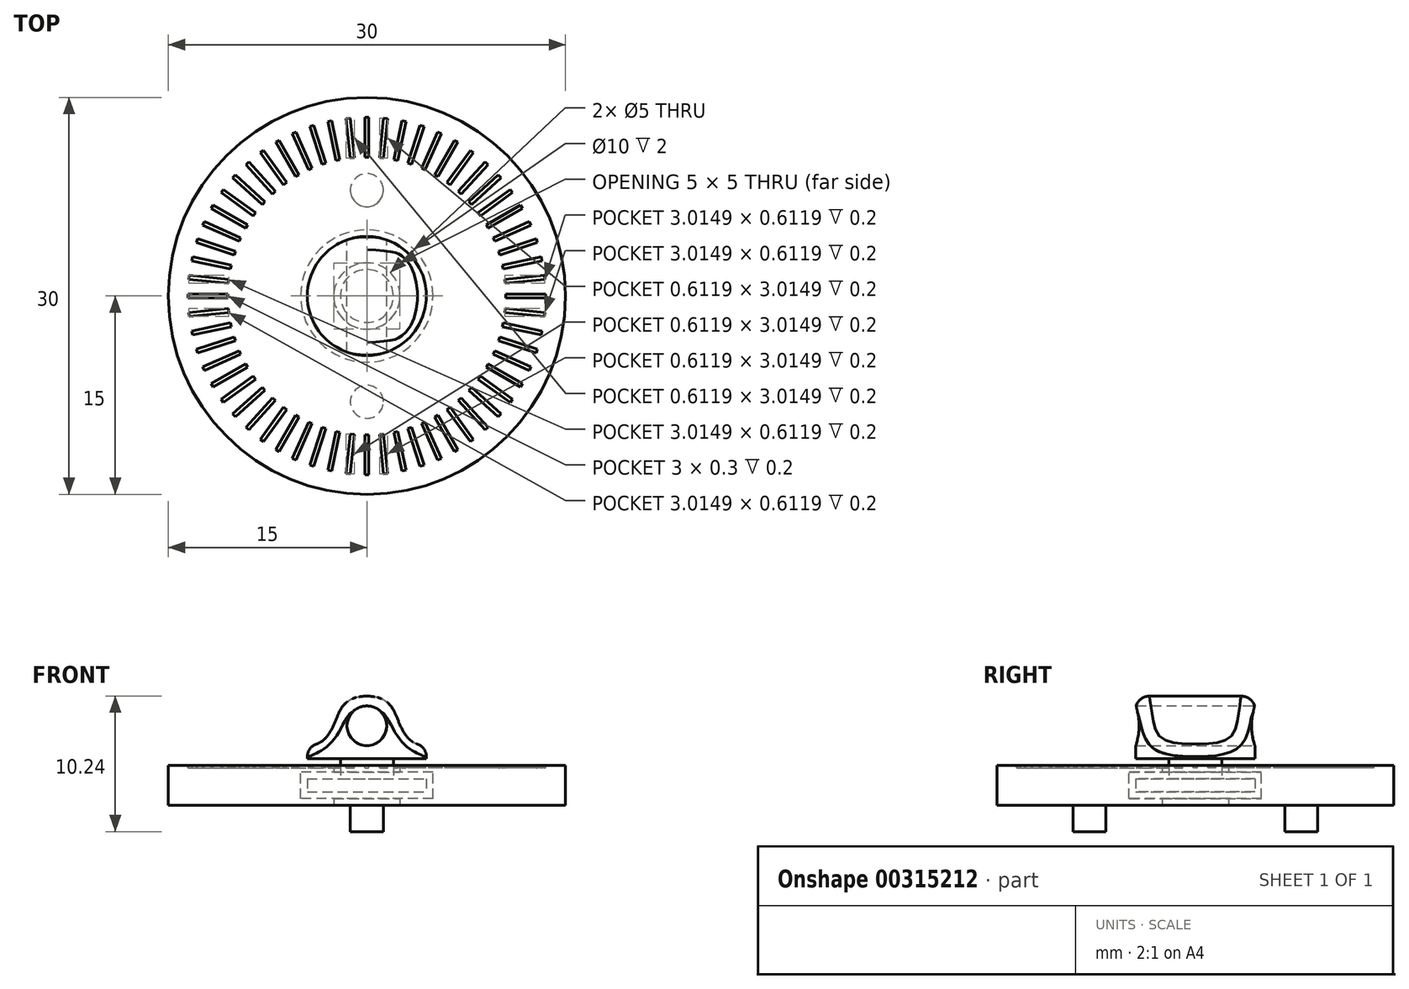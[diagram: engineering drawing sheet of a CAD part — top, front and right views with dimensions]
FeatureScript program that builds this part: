
annotation { "Feature Type Name" : "Feature", "Feature Type Description" : "" }
export const myFeature = defineFeature(function(context is Context, id is Id, definition is map)
    precondition{}
    {
        {
            var Q0;
            Q0=qCreatedBy(makeId("Top.planeOp"),FACE);
            var sketch = newSketch(context, id + "F0", { "sketchPlane" : qUnion([Q0])});
            skCircle(sketch, "E0", {"center": v(0, 0) * mm, "radius": 15 * mm});
            skCircle(sketch, "E1", {"center": v(0, 0) * mm, "radius": 2.5 * mm});
            skSolve(sketch);
        }
        {
            var Q0;
            Q0=makeQuery(id+"F0.imprint","IMPRINT",FACE,{"disambiguationData":[TD([[makeQuery(id+"F0.imprint","IMPRINT",EDGE,{"derivedFrom":sQuery(id+"F0.wireOp",EDGE,"E0")}),1.0]])]});
            extrude(context, id + "F1", {"entities" : qUnion([Q0]), "depth" : 3 * mm, "offsetDistance" : 25 * mm});
        }
        {
            var Q0;
            Q0=qCreatedBy(makeId("Front.planeOp"),FACE);
            var sketch = newSketch(context, id + "F2", { "sketchPlane" : qUnion([Q0])});
            skLineSegment(sketch, "E2.0", {"start": v(-2.5, 3) * mm, "end": v(2.5, 3) * mm, "construction": true});
            skLineSegment(sketch, "E3.0", {"start": v(-2.5, 0) * mm, "end": v(2.5, 0) * mm, "construction": true});
            skLineSegment(sketch, "E4", {"start": v(0, 0) * mm, "end": v(0, 16.06) * mm, "construction": true});
            skLineSegment(sketch, "E5", {"start": v(-2, 2) * mm, "end": v(-4.5, 2) * mm});
            skLineSegment(sketch, "E6", {"start": v(-4.5, 2) * mm, "end": v(-4.5, 1) * mm});
            skLineSegment(sketch, "E7", {"start": v(-4.5, 1) * mm, "end": v(0, 1) * mm});
            skLineSegment(sketch, "E8", {"start": v(-2, 2) * mm, "end": v(-2, 3.5) * mm});
            skLineSegment(sketch, "E9", {"start": v(0, 1) * mm, "end": v(0, 0) * mm, "construction": true});
            skLineSegment(sketch, "E10", {"start": v(-2, 3.5) * mm, "end": v(-4.5, 3.5) * mm});
            skLineSegment(sketch, "E11", {"start": v(-4.5, 3.5) * mm, "end": v(-4.5, 4.5) * mm});
            skLineSegment(sketch, "E12", {"start": v(-4.5, 4.5) * mm, "end": v(0, 4.5) * mm});
            skLineSegment(sketch, "E13", {"start": v(0, 4.5) * mm, "end": v(0, 1) * mm});
            skLineSegment(sketch, "E14", {"start": v(-4.5, 3.5) * mm, "end": v(-4.5, 3) * mm, "construction": true});
            skSolve(sketch);
        }
        {
            var Q0;
            Q0=qCreatedBy(makeId("Front.planeOp"),FACE);
            var sketch = newSketch(context, id + "F3", { "sketchPlane" : qUnion([Q0])});
            skLineSegment(sketch, "E15.0", {"start": v(-2, 2) * mm, "end": v(-2, 3.5) * mm, "construction": true});
            skLineSegment(sketch, "E16", {"start": v(-2, 2.5) * mm, "end": v(-5, 2.5) * mm});
            skLineSegment(sketch, "E17", {"start": v(-5, 2.5) * mm, "end": v(-5, 0.5) * mm});
            skLineSegment(sketch, "E18", {"start": v(-5, 0.5) * mm, "end": v(0, 0.5) * mm});
            skLineSegment(sketch, "E19", {"start": v(-2, 2.5) * mm, "end": v(-2, 2) * mm});
            skLineSegment(sketch, "E20.0", {"start": v(0, 0) * mm, "end": v(0, 16.06) * mm, "construction": true});
            skLineSegment(sketch, "E21", {"start": v(-2, 2.5) * mm, "end": v(0, 2.5) * mm});
            skLineSegment(sketch, "E22", {"start": v(0, 2.5) * mm, "end": v(0, 0.5) * mm});
            skSolve(sketch);
        }
        {
            var Q0;
            Q0=makeQuery(id+"F3.imprint","IMPRINT",FACE,{"disambiguationData":[TD([[makeQuery(id+"F3.imprint","IMPRINT",EDGE,{"derivedFrom":sQuery(id+"F3.wireOp",EDGE,"E16")}),1.0]])]});
            var Q1;
            Q1=sQuery(id+"F2.wireOp",EDGE,"E4");
            revolve(context, id + "F4", {"operationType" : NewBodyOperationType.REMOVE, "surfaceOperationType" : NewSurfaceOperationType.NEW, "entities" : qUnion([Q0]), "axis" : qUnion([Q1]), "revolveType" : RevolveType.FULL, "oppositeDirection" : true});
        }
        {
            var Q0;
            Q0=makeQuery(id+"F2.imprint","IMPRINT",FACE,{"disambiguationData":[TD([[makeQuery(id+"F2.imprint","IMPRINT",EDGE,{"derivedFrom":sQuery(id+"F2.wireOp",EDGE,"E5")}),1.0]])]});
            var Q1;
            Q1=sQuery(id+"F2.wireOp",EDGE,"E4");
            revolve(context, id + "F5", {"surfaceOperationType" : NewSurfaceOperationType.NEW, "entities" : qUnion([Q0]), "axis" : qUnion([Q1]), "revolveType" : RevolveType.FULL});
        }
        {
            var Q0;
            Q0=qCreatedBy(makeId("Front.planeOp"),FACE);
            var sketch = newSketch(context, id + "F6", { "sketchPlane" : qUnion([Q0])});
            skLineSegment(sketch, "E23.0", {"start": v(4.5, 4.5) * mm, "end": v(-4.5, 4.5) * mm});
            skCircle(sketch, "E24", {"center": v(0, 6) * mm, "radius": 1.5 * mm});
            skLineSegment(sketch, "E25.0", {"start": v(0, 0) * mm, "end": v(0, 16.06) * mm, "construction": true});
            skFitSpline(sketch, "E26", {"points": [v(0, 8.24) * mm, v(-2.5, 6.08) * mm, v(-4.5, 4.5) * mm], "startDerivative": vector(-10.34, 0) * mm, "endDerivative": vector(-7.09, 0) * mm});
            skLineSegment(sketch, "E27", {"start": v(0, 8.24) * mm, "end": v(-1.84, 8.24) * mm, "construction": true});
            skFitSpline(sketch, "E28.MirrorCS", {"points": [v(0, 8.24) * mm, v(2.5, 6.08) * mm, v(4.5, 4.5) * mm], "startDerivative": vector(10.34, 0) * mm, "endDerivative": vector(7.09, 0) * mm});
            skLineSegment(sketch, "E29.bottom", {"start": v(-1.1, 4.5) * mm, "end": v(1.14, 4.5) * mm});
            skLineSegment(sketch, "E29.top", {"start": v(-1.1, 3.86) * mm, "end": v(1.14, 3.86) * mm});
            skLineSegment(sketch, "E29.left", {"start": v(-1.1, 4.5) * mm, "end": v(-1.1, 3.86) * mm});
            skLineSegment(sketch, "E29.right", {"start": v(1.14, 4.5) * mm, "end": v(1.14, 3.86) * mm});
            skSolve(sketch);
        }
        {
            var Q0;
            {var subQ1=sQuery(id+"F6.wireOp",EDGE,"E24");Q0=makeQuery(id+"F6.imprint","IMPRINT",FACE,{"disambiguationData":[TD([[makeQuery(id+"F6.imprint","IMPRINT",EDGE,{"derivedFrom":subQ1}),-1.0]])]});}
            var Q1;
            Q1=makeQuery(id+"F6.imprint","IMPRINT",FACE,{"disambiguationData":[TD([[makeQuery(id+"F6.imprint","IMPRINT",EDGE,{"derivedFrom":sQuery(id+"F6.wireOp",EDGE,"E29.top")}),1.0]])]});
            var Q2;
            Q2=makeQuery(id+"F5.opRevolve","SWEPT_FACE",FACE,{"disambiguationData":[OSD([sQuery(id+"F2.wireOp",EDGE,"E11")])]});
            var Q3;
            Q3=makeQuery(id+"F5.opRevolve","SWEPT_FACE",FACE,{"disambiguationData":[OSD([sQuery(id+"F2.wireOp",EDGE,"E11")])]});
            extrude(context, id + "F7", {"entities" : qUnion([Q0, Q1]), "operationType" : NewBodyOperationType.ADD, "endBound" : BoundingType.UP_TO_SURFACE, "depth" : 25 * mm, "endBoundEntityFace" : qUnion([Q2]), "offsetDistance" : 25 * mm, "hasSecondDirection" : true, "secondDirectionBound" : BoundingType.UP_TO_SURFACE, "secondDirectionOppositeDirection" : true, "secondDirectionDepth" : 25 * mm, "secondDirectionBoundEntityFace" : qUnion([Q3])});
        }
        {
            var Q0;
            Q0=makeQuery(id+"F1.opExtrude","CAP_FACE",FACE,{"disambiguationData":[OSD([sQuery(id+"F0.wireOp",EDGE,"E0"),sQuery(id+"F0.wireOp",EDGE,"E1")])],"isStart":false});
            var sketch = newSketch(context, id + "F8", { "sketchPlane" : qUnion([Q0])});
            skLineSegment(sketch, "E30.bottom", {"start": v(-0.15, 13.5) * mm, "end": v(0.15, 13.5) * mm});
            skLineSegment(sketch, "E30.top", {"start": v(-0.15, 10.5) * mm, "end": v(0.15, 10.5) * mm});
            skLineSegment(sketch, "E30.left", {"start": v(-0.15, 13.5) * mm, "end": v(-0.15, 10.5) * mm});
            skLineSegment(sketch, "E30.right", {"start": v(0.15, 13.5) * mm, "end": v(0.15, 10.5) * mm});
            skPoint(sketch, "E31", {"position": v(0, 13.5) * mm});
            skLineSegment(sketch, "E32.1.0", {"start": v(-1.56, 13.41) * mm, "end": v(-1.25, 10.43) * mm});
            skLineSegment(sketch, "E32.1.1", {"start": v(-1.26, 13.44) * mm, "end": v(-0.95, 10.46) * mm});
            skPoint(sketch, "E32.1.2", {"position": v(-1.41, 13.43) * mm});
            skLineSegment(sketch, "E32.1.3", {"start": v(-1.56, 13.41) * mm, "end": v(-1.26, 13.44) * mm});
            skLineSegment(sketch, "E32.1.4", {"start": v(-1.25, 10.43) * mm, "end": v(-0.95, 10.46) * mm});
            skLineSegment(sketch, "E32.2.0", {"start": v(-2.95, 13.17) * mm, "end": v(-2.33, 10.24) * mm});
            skLineSegment(sketch, "E32.2.1", {"start": v(-2.66, 13.24) * mm, "end": v(-2.04, 10.3) * mm});
            skPoint(sketch, "E32.2.2", {"position": v(-2.8, 13.2) * mm});
            skLineSegment(sketch, "E32.2.3", {"start": v(-2.95, 13.17) * mm, "end": v(-2.66, 13.24) * mm});
            skLineSegment(sketch, "E32.2.4", {"start": v(-2.33, 10.24) * mm, "end": v(-2.04, 10.3) * mm});
            skPoint(sketch, "E32.center", {"position": v(0, 0) * mm});
            skLineSegment(sketch, "E33.2.3.0", {"start": v(-4.31, 12.8) * mm, "end": v(-3.39, 9.94) * mm});
            skLineSegment(sketch, "E33.3.3.0", {"start": v(-4.03, 12.89) * mm, "end": v(-3.1, 10.03) * mm});
            skPoint(sketch, "E33.6.3.0", {"position": v(-4.17, 12.84) * mm});
            skLineSegment(sketch, "E33.7.3.0", {"start": v(-4.31, 12.8) * mm, "end": v(-4.03, 12.89) * mm});
            skLineSegment(sketch, "E33.10.3.0", {"start": v(-3.39, 9.94) * mm, "end": v(-3.1, 10.03) * mm});
            skLineSegment(sketch, "E33.2.4.0", {"start": v(-5.63, 12.27) * mm, "end": v(-4.4, 9.53) * mm});
            skLineSegment(sketch, "E33.3.4.0", {"start": v(-5.35, 12.4) * mm, "end": v(-4.13, 9.65) * mm});
            skPoint(sketch, "E33.6.4.0", {"position": v(-5.5, 12.33) * mm});
            skLineSegment(sketch, "E33.7.4.0", {"start": v(-5.63, 12.27) * mm, "end": v(-5.35, 12.4) * mm});
            skLineSegment(sketch, "E33.10.4.0", {"start": v(-4.4, 9.53) * mm, "end": v(-4.13, 9.65) * mm});
            skLineSegment(sketch, "E33.2.5.0", {"start": v(-6.88, 11.62) * mm, "end": v(-5.38, 9.02) * mm});
            skLineSegment(sketch, "E33.3.5.0", {"start": v(-6.62, 11.77) * mm, "end": v(-5.12, 9.17) * mm});
            skPoint(sketch, "E33.6.5.0", {"position": v(-6.75, 11.7) * mm});
            skLineSegment(sketch, "E33.7.5.0", {"start": v(-6.88, 11.62) * mm, "end": v(-6.62, 11.77) * mm});
            skLineSegment(sketch, "E33.10.5.0", {"start": v(-5.38, 9.02) * mm, "end": v(-5.12, 9.17) * mm});
            skLineSegment(sketch, "E33.2.6.0", {"start": v(-8.06, 10.83) * mm, "end": v(-6.3, 8.4) * mm});
            skLineSegment(sketch, "E33.3.6.0", {"start": v(-7.81, 11) * mm, "end": v(-6.05, 8.58) * mm});
            skPoint(sketch, "E33.6.6.0", {"position": v(-7.94, 10.92) * mm});
            skLineSegment(sketch, "E33.7.6.0", {"start": v(-8.06, 10.83) * mm, "end": v(-7.81, 11) * mm});
            skLineSegment(sketch, "E33.10.6.0", {"start": v(-6.3, 8.4) * mm, "end": v(-6.05, 8.58) * mm});
            skLineSegment(sketch, "E33.2.7.0", {"start": v(-9.14, 9.93) * mm, "end": v(-7.14, 7.7) * mm});
            skLineSegment(sketch, "E33.3.7.0", {"start": v(-8.92, 10.13) * mm, "end": v(-6.91, 7.9) * mm});
            skPoint(sketch, "E33.6.7.0", {"position": v(-9.03, 10.03) * mm});
            skLineSegment(sketch, "E33.7.7.0", {"start": v(-9.14, 9.93) * mm, "end": v(-8.92, 10.13) * mm});
            skLineSegment(sketch, "E33.10.7.0", {"start": v(-7.14, 7.7) * mm, "end": v(-6.91, 7.9) * mm});
            skLineSegment(sketch, "E33.2.8.0", {"start": v(-10.13, 8.92) * mm, "end": v(-7.9, 6.91) * mm});
            skLineSegment(sketch, "E33.3.8.0", {"start": v(-9.93, 9.14) * mm, "end": v(-7.7, 7.14) * mm});
            skPoint(sketch, "E33.6.8.0", {"position": v(-10.03, 9.03) * mm});
            skLineSegment(sketch, "E33.7.8.0", {"start": v(-10.13, 8.92) * mm, "end": v(-9.93, 9.14) * mm});
            skLineSegment(sketch, "E33.10.8.0", {"start": v(-7.9, 6.91) * mm, "end": v(-7.7, 7.14) * mm});
            skLineSegment(sketch, "E33.2.9.0", {"start": v(-11, 7.81) * mm, "end": v(-8.58, 6.05) * mm});
            skLineSegment(sketch, "E33.3.9.0", {"start": v(-10.83, 8.06) * mm, "end": v(-8.4, 6.3) * mm});
            skPoint(sketch, "E33.6.9.0", {"position": v(-10.92, 7.94) * mm});
            skLineSegment(sketch, "E33.7.9.0", {"start": v(-11, 7.81) * mm, "end": v(-10.83, 8.06) * mm});
            skLineSegment(sketch, "E33.10.9.0", {"start": v(-8.58, 6.05) * mm, "end": v(-8.4, 6.3) * mm});
            skLineSegment(sketch, "E34.2.10.0", {"start": v(-11.77, 6.62) * mm, "end": v(-9.17, 5.12) * mm});
            skLineSegment(sketch, "E34.3.10.0", {"start": v(-11.62, 6.88) * mm, "end": v(-9.02, 5.38) * mm});
            skPoint(sketch, "E34.6.10.0", {"position": v(-11.7, 6.75) * mm});
            skLineSegment(sketch, "E34.7.10.0", {"start": v(-11.77, 6.62) * mm, "end": v(-11.62, 6.88) * mm});
            skLineSegment(sketch, "E34.10.10.0", {"start": v(-9.17, 5.12) * mm, "end": v(-9.02, 5.38) * mm});
            skLineSegment(sketch, "E34.2.11.0", {"start": v(-12.4, 5.35) * mm, "end": v(-9.65, 4.13) * mm});
            skLineSegment(sketch, "E34.3.11.0", {"start": v(-12.27, 5.63) * mm, "end": v(-9.53, 4.4) * mm});
            skPoint(sketch, "E34.6.11.0", {"position": v(-12.33, 5.5) * mm});
            skLineSegment(sketch, "E34.7.11.0", {"start": v(-12.4, 5.35) * mm, "end": v(-12.27, 5.63) * mm});
            skLineSegment(sketch, "E34.10.11.0", {"start": v(-9.65, 4.13) * mm, "end": v(-9.53, 4.4) * mm});
            skLineSegment(sketch, "E34.2.12.0", {"start": v(-12.89, 4.03) * mm, "end": v(-10.03, 3.1) * mm});
            skLineSegment(sketch, "E34.3.12.0", {"start": v(-12.8, 4.31) * mm, "end": v(-9.94, 3.39) * mm});
            skPoint(sketch, "E34.6.12.0", {"position": v(-12.84, 4.17) * mm});
            skLineSegment(sketch, "E34.7.12.0", {"start": v(-12.89, 4.03) * mm, "end": v(-12.8, 4.31) * mm});
            skLineSegment(sketch, "E34.10.12.0", {"start": v(-10.03, 3.1) * mm, "end": v(-9.94, 3.39) * mm});
            skLineSegment(sketch, "E34.2.13.0", {"start": v(-13.24, 2.66) * mm, "end": v(-10.3, 2.04) * mm});
            skLineSegment(sketch, "E34.3.13.0", {"start": v(-13.17, 2.95) * mm, "end": v(-10.24, 2.33) * mm});
            skPoint(sketch, "E34.6.13.0", {"position": v(-13.2, 2.8) * mm});
            skLineSegment(sketch, "E34.7.13.0", {"start": v(-13.24, 2.66) * mm, "end": v(-13.17, 2.95) * mm});
            skLineSegment(sketch, "E34.10.13.0", {"start": v(-10.3, 2.04) * mm, "end": v(-10.24, 2.33) * mm});
            skLineSegment(sketch, "E34.2.14.0", {"start": v(-13.44, 1.26) * mm, "end": v(-10.46, 0.95) * mm});
            skLineSegment(sketch, "E34.3.14.0", {"start": v(-13.41, 1.56) * mm, "end": v(-10.43, 1.25) * mm});
            skPoint(sketch, "E34.6.14.0", {"position": v(-13.43, 1.41) * mm});
            skLineSegment(sketch, "E34.7.14.0", {"start": v(-13.44, 1.26) * mm, "end": v(-13.41, 1.56) * mm});
            skLineSegment(sketch, "E34.10.14.0", {"start": v(-10.46, 0.95) * mm, "end": v(-10.43, 1.25) * mm});
            skLineSegment(sketch, "E34.2.15.0", {"start": v(-13.5, -0.15) * mm, "end": v(-10.5, -0.15) * mm});
            skLineSegment(sketch, "E34.3.15.0", {"start": v(-13.5, 0.15) * mm, "end": v(-10.5, 0.15) * mm});
            skPoint(sketch, "E34.6.15.0", {"position": v(-13.5, 0) * mm});
            skLineSegment(sketch, "E34.7.15.0", {"start": v(-13.5, -0.15) * mm, "end": v(-13.5, 0.15) * mm});
            skLineSegment(sketch, "E34.10.15.0", {"start": v(-10.5, -0.15) * mm, "end": v(-10.5, 0.15) * mm});
            skLineSegment(sketch, "E34.2.16.0", {"start": v(-13.41, -1.56) * mm, "end": v(-10.43, -1.25) * mm});
            skLineSegment(sketch, "E34.3.16.0", {"start": v(-13.44, -1.26) * mm, "end": v(-10.46, -0.95) * mm});
            skPoint(sketch, "E34.6.16.0", {"position": v(-13.43, -1.41) * mm});
            skLineSegment(sketch, "E34.7.16.0", {"start": v(-13.41, -1.56) * mm, "end": v(-13.44, -1.26) * mm});
            skLineSegment(sketch, "E34.10.16.0", {"start": v(-10.43, -1.25) * mm, "end": v(-10.46, -0.95) * mm});
            skLineSegment(sketch, "E34.2.17.0", {"start": v(-13.17, -2.95) * mm, "end": v(-10.24, -2.33) * mm});
            skLineSegment(sketch, "E34.3.17.0", {"start": v(-13.24, -2.66) * mm, "end": v(-10.3, -2.04) * mm});
            skPoint(sketch, "E34.6.17.0", {"position": v(-13.2, -2.8) * mm});
            skLineSegment(sketch, "E34.7.17.0", {"start": v(-13.17, -2.95) * mm, "end": v(-13.24, -2.66) * mm});
            skLineSegment(sketch, "E34.10.17.0", {"start": v(-10.24, -2.33) * mm, "end": v(-10.3, -2.04) * mm});
            skLineSegment(sketch, "E34.2.18.0", {"start": v(-12.8, -4.31) * mm, "end": v(-9.94, -3.39) * mm});
            skLineSegment(sketch, "E34.3.18.0", {"start": v(-12.89, -4.03) * mm, "end": v(-10.03, -3.1) * mm});
            skPoint(sketch, "E34.6.18.0", {"position": v(-12.84, -4.17) * mm});
            skLineSegment(sketch, "E34.7.18.0", {"start": v(-12.8, -4.31) * mm, "end": v(-12.89, -4.03) * mm});
            skLineSegment(sketch, "E34.10.18.0", {"start": v(-9.94, -3.39) * mm, "end": v(-10.03, -3.1) * mm});
            skLineSegment(sketch, "E34.2.19.0", {"start": v(-12.27, -5.63) * mm, "end": v(-9.53, -4.4) * mm});
            skLineSegment(sketch, "E34.3.19.0", {"start": v(-12.4, -5.35) * mm, "end": v(-9.65, -4.13) * mm});
            skPoint(sketch, "E34.6.19.0", {"position": v(-12.33, -5.5) * mm});
            skLineSegment(sketch, "E34.7.19.0", {"start": v(-12.27, -5.63) * mm, "end": v(-12.4, -5.35) * mm});
            skLineSegment(sketch, "E34.10.19.0", {"start": v(-9.53, -4.4) * mm, "end": v(-9.65, -4.13) * mm});
            skLineSegment(sketch, "E35.2.20.0", {"start": v(-11.62, -6.88) * mm, "end": v(-9.02, -5.38) * mm});
            skLineSegment(sketch, "E35.3.20.0", {"start": v(-11.77, -6.62) * mm, "end": v(-9.17, -5.12) * mm});
            skPoint(sketch, "E35.6.20.0", {"position": v(-11.7, -6.75) * mm});
            skLineSegment(sketch, "E35.7.20.0", {"start": v(-11.62, -6.88) * mm, "end": v(-11.77, -6.62) * mm});
            skLineSegment(sketch, "E35.10.20.0", {"start": v(-9.02, -5.38) * mm, "end": v(-9.17, -5.12) * mm});
            skLineSegment(sketch, "E35.2.21.0", {"start": v(-10.83, -8.06) * mm, "end": v(-8.4, -6.3) * mm});
            skLineSegment(sketch, "E35.3.21.0", {"start": v(-11, -7.81) * mm, "end": v(-8.58, -6.05) * mm});
            skPoint(sketch, "E35.6.21.0", {"position": v(-10.92, -7.94) * mm});
            skLineSegment(sketch, "E35.7.21.0", {"start": v(-10.83, -8.06) * mm, "end": v(-11, -7.81) * mm});
            skLineSegment(sketch, "E35.10.21.0", {"start": v(-8.4, -6.3) * mm, "end": v(-8.58, -6.05) * mm});
            skLineSegment(sketch, "E35.2.22.0", {"start": v(-9.93, -9.14) * mm, "end": v(-7.7, -7.14) * mm});
            skLineSegment(sketch, "E35.3.22.0", {"start": v(-10.13, -8.92) * mm, "end": v(-7.9, -6.91) * mm});
            skPoint(sketch, "E35.6.22.0", {"position": v(-10.03, -9.03) * mm});
            skLineSegment(sketch, "E35.7.22.0", {"start": v(-9.93, -9.14) * mm, "end": v(-10.13, -8.92) * mm});
            skLineSegment(sketch, "E35.10.22.0", {"start": v(-7.7, -7.14) * mm, "end": v(-7.9, -6.91) * mm});
            skLineSegment(sketch, "E35.2.23.0", {"start": v(-8.92, -10.13) * mm, "end": v(-6.91, -7.9) * mm});
            skLineSegment(sketch, "E35.3.23.0", {"start": v(-9.14, -9.93) * mm, "end": v(-7.14, -7.7) * mm});
            skPoint(sketch, "E35.6.23.0", {"position": v(-9.03, -10.03) * mm});
            skLineSegment(sketch, "E35.7.23.0", {"start": v(-8.92, -10.13) * mm, "end": v(-9.14, -9.93) * mm});
            skLineSegment(sketch, "E35.10.23.0", {"start": v(-6.91, -7.9) * mm, "end": v(-7.14, -7.7) * mm});
            skLineSegment(sketch, "E35.2.24.0", {"start": v(-7.81, -11) * mm, "end": v(-6.05, -8.58) * mm});
            skLineSegment(sketch, "E35.3.24.0", {"start": v(-8.06, -10.83) * mm, "end": v(-6.3, -8.4) * mm});
            skPoint(sketch, "E35.6.24.0", {"position": v(-7.94, -10.92) * mm});
            skLineSegment(sketch, "E35.7.24.0", {"start": v(-7.81, -11) * mm, "end": v(-8.06, -10.83) * mm});
            skLineSegment(sketch, "E35.10.24.0", {"start": v(-6.05, -8.58) * mm, "end": v(-6.3, -8.4) * mm});
            skLineSegment(sketch, "E35.2.25.0", {"start": v(-6.62, -11.77) * mm, "end": v(-5.12, -9.17) * mm});
            skLineSegment(sketch, "E35.3.25.0", {"start": v(-6.88, -11.62) * mm, "end": v(-5.38, -9.02) * mm});
            skPoint(sketch, "E35.6.25.0", {"position": v(-6.75, -11.7) * mm});
            skLineSegment(sketch, "E35.7.25.0", {"start": v(-6.62, -11.77) * mm, "end": v(-6.88, -11.62) * mm});
            skLineSegment(sketch, "E35.10.25.0", {"start": v(-5.12, -9.17) * mm, "end": v(-5.38, -9.02) * mm});
            skLineSegment(sketch, "E35.2.26.0", {"start": v(-5.35, -12.4) * mm, "end": v(-4.13, -9.65) * mm});
            skLineSegment(sketch, "E35.3.26.0", {"start": v(-5.63, -12.27) * mm, "end": v(-4.4, -9.53) * mm});
            skPoint(sketch, "E35.6.26.0", {"position": v(-5.5, -12.33) * mm});
            skLineSegment(sketch, "E35.7.26.0", {"start": v(-5.35, -12.4) * mm, "end": v(-5.63, -12.27) * mm});
            skLineSegment(sketch, "E35.10.26.0", {"start": v(-4.13, -9.65) * mm, "end": v(-4.4, -9.53) * mm});
            skLineSegment(sketch, "E35.2.27.0", {"start": v(-4.03, -12.89) * mm, "end": v(-3.1, -10.03) * mm});
            skLineSegment(sketch, "E35.3.27.0", {"start": v(-4.31, -12.8) * mm, "end": v(-3.39, -9.94) * mm});
            skPoint(sketch, "E35.6.27.0", {"position": v(-4.17, -12.84) * mm});
            skLineSegment(sketch, "E35.7.27.0", {"start": v(-4.03, -12.89) * mm, "end": v(-4.31, -12.8) * mm});
            skLineSegment(sketch, "E35.10.27.0", {"start": v(-3.1, -10.03) * mm, "end": v(-3.39, -9.94) * mm});
            skLineSegment(sketch, "E35.2.28.0", {"start": v(-2.66, -13.24) * mm, "end": v(-2.04, -10.3) * mm});
            skLineSegment(sketch, "E35.3.28.0", {"start": v(-2.95, -13.17) * mm, "end": v(-2.33, -10.24) * mm});
            skPoint(sketch, "E35.6.28.0", {"position": v(-2.8, -13.2) * mm});
            skLineSegment(sketch, "E35.7.28.0", {"start": v(-2.66, -13.24) * mm, "end": v(-2.95, -13.17) * mm});
            skLineSegment(sketch, "E35.10.28.0", {"start": v(-2.04, -10.3) * mm, "end": v(-2.33, -10.24) * mm});
            skLineSegment(sketch, "E35.2.29.0", {"start": v(-1.26, -13.44) * mm, "end": v(-0.95, -10.46) * mm});
            skLineSegment(sketch, "E35.3.29.0", {"start": v(-1.56, -13.41) * mm, "end": v(-1.25, -10.43) * mm});
            skPoint(sketch, "E35.6.29.0", {"position": v(-1.41, -13.43) * mm});
            skLineSegment(sketch, "E35.7.29.0", {"start": v(-1.26, -13.44) * mm, "end": v(-1.56, -13.41) * mm});
            skLineSegment(sketch, "E35.10.29.0", {"start": v(-0.95, -10.46) * mm, "end": v(-1.25, -10.43) * mm});
            skLineSegment(sketch, "E36.2.30.0", {"start": v(0.15, -13.5) * mm, "end": v(0.15, -10.5) * mm});
            skLineSegment(sketch, "E36.3.30.0", {"start": v(-0.15, -13.5) * mm, "end": v(-0.15, -10.5) * mm});
            skPoint(sketch, "E36.6.30.0", {"position": v(0, -13.5) * mm});
            skLineSegment(sketch, "E36.7.30.0", {"start": v(0.15, -13.5) * mm, "end": v(-0.15, -13.5) * mm});
            skLineSegment(sketch, "E36.10.30.0", {"start": v(0.15, -10.5) * mm, "end": v(-0.15, -10.5) * mm});
            skLineSegment(sketch, "E36.2.31.0", {"start": v(1.56, -13.41) * mm, "end": v(1.25, -10.43) * mm});
            skLineSegment(sketch, "E36.3.31.0", {"start": v(1.26, -13.44) * mm, "end": v(0.95, -10.46) * mm});
            skPoint(sketch, "E36.6.31.0", {"position": v(1.41, -13.43) * mm});
            skLineSegment(sketch, "E36.7.31.0", {"start": v(1.56, -13.41) * mm, "end": v(1.26, -13.44) * mm});
            skLineSegment(sketch, "E36.10.31.0", {"start": v(1.25, -10.43) * mm, "end": v(0.95, -10.46) * mm});
            skLineSegment(sketch, "E36.2.32.0", {"start": v(2.95, -13.17) * mm, "end": v(2.33, -10.24) * mm});
            skLineSegment(sketch, "E36.3.32.0", {"start": v(2.66, -13.24) * mm, "end": v(2.04, -10.3) * mm});
            skPoint(sketch, "E36.6.32.0", {"position": v(2.8, -13.2) * mm});
            skLineSegment(sketch, "E36.7.32.0", {"start": v(2.95, -13.17) * mm, "end": v(2.66, -13.24) * mm});
            skLineSegment(sketch, "E36.10.32.0", {"start": v(2.33, -10.24) * mm, "end": v(2.04, -10.3) * mm});
            skLineSegment(sketch, "E36.2.33.0", {"start": v(4.31, -12.8) * mm, "end": v(3.39, -9.94) * mm});
            skLineSegment(sketch, "E36.3.33.0", {"start": v(4.03, -12.89) * mm, "end": v(3.1, -10.03) * mm});
            skPoint(sketch, "E36.6.33.0", {"position": v(4.17, -12.84) * mm});
            skLineSegment(sketch, "E36.7.33.0", {"start": v(4.31, -12.8) * mm, "end": v(4.03, -12.89) * mm});
            skLineSegment(sketch, "E36.10.33.0", {"start": v(3.39, -9.94) * mm, "end": v(3.1, -10.03) * mm});
            skLineSegment(sketch, "E36.2.34.0", {"start": v(5.63, -12.27) * mm, "end": v(4.4, -9.53) * mm});
            skLineSegment(sketch, "E36.3.34.0", {"start": v(5.35, -12.4) * mm, "end": v(4.13, -9.65) * mm});
            skPoint(sketch, "E36.6.34.0", {"position": v(5.5, -12.33) * mm});
            skLineSegment(sketch, "E36.7.34.0", {"start": v(5.63, -12.27) * mm, "end": v(5.35, -12.4) * mm});
            skLineSegment(sketch, "E36.10.34.0", {"start": v(4.4, -9.53) * mm, "end": v(4.13, -9.65) * mm});
            skLineSegment(sketch, "E36.2.35.0", {"start": v(6.88, -11.62) * mm, "end": v(5.38, -9.02) * mm});
            skLineSegment(sketch, "E36.3.35.0", {"start": v(6.62, -11.77) * mm, "end": v(5.12, -9.17) * mm});
            skPoint(sketch, "E36.6.35.0", {"position": v(6.75, -11.7) * mm});
            skLineSegment(sketch, "E36.7.35.0", {"start": v(6.88, -11.62) * mm, "end": v(6.62, -11.77) * mm});
            skLineSegment(sketch, "E36.10.35.0", {"start": v(5.38, -9.02) * mm, "end": v(5.12, -9.17) * mm});
            skLineSegment(sketch, "E36.2.36.0", {"start": v(8.06, -10.83) * mm, "end": v(6.3, -8.4) * mm});
            skLineSegment(sketch, "E36.3.36.0", {"start": v(7.81, -11) * mm, "end": v(6.05, -8.58) * mm});
            skPoint(sketch, "E36.6.36.0", {"position": v(7.94, -10.92) * mm});
            skLineSegment(sketch, "E36.7.36.0", {"start": v(8.06, -10.83) * mm, "end": v(7.81, -11) * mm});
            skLineSegment(sketch, "E36.10.36.0", {"start": v(6.3, -8.4) * mm, "end": v(6.05, -8.58) * mm});
            skLineSegment(sketch, "E36.2.37.0", {"start": v(9.14, -9.93) * mm, "end": v(7.14, -7.7) * mm});
            skLineSegment(sketch, "E36.3.37.0", {"start": v(8.92, -10.13) * mm, "end": v(6.91, -7.9) * mm});
            skPoint(sketch, "E36.6.37.0", {"position": v(9.03, -10.03) * mm});
            skLineSegment(sketch, "E36.7.37.0", {"start": v(9.14, -9.93) * mm, "end": v(8.92, -10.13) * mm});
            skLineSegment(sketch, "E36.10.37.0", {"start": v(7.14, -7.7) * mm, "end": v(6.91, -7.9) * mm});
            skLineSegment(sketch, "E36.2.38.0", {"start": v(10.13, -8.92) * mm, "end": v(7.9, -6.91) * mm});
            skLineSegment(sketch, "E36.3.38.0", {"start": v(9.93, -9.14) * mm, "end": v(7.7, -7.14) * mm});
            skPoint(sketch, "E36.6.38.0", {"position": v(10.03, -9.03) * mm});
            skLineSegment(sketch, "E36.7.38.0", {"start": v(10.13, -8.92) * mm, "end": v(9.93, -9.14) * mm});
            skLineSegment(sketch, "E36.10.38.0", {"start": v(7.9, -6.91) * mm, "end": v(7.7, -7.14) * mm});
            skLineSegment(sketch, "E36.2.39.0", {"start": v(11, -7.81) * mm, "end": v(8.58, -6.05) * mm});
            skLineSegment(sketch, "E36.3.39.0", {"start": v(10.83, -8.06) * mm, "end": v(8.4, -6.3) * mm});
            skPoint(sketch, "E36.6.39.0", {"position": v(10.92, -7.94) * mm});
            skLineSegment(sketch, "E36.7.39.0", {"start": v(11, -7.81) * mm, "end": v(10.83, -8.06) * mm});
            skLineSegment(sketch, "E36.10.39.0", {"start": v(8.58, -6.05) * mm, "end": v(8.4, -6.3) * mm});
            skLineSegment(sketch, "E37.2.40.0", {"start": v(11.77, -6.62) * mm, "end": v(9.17, -5.12) * mm});
            skLineSegment(sketch, "E37.3.40.0", {"start": v(11.62, -6.88) * mm, "end": v(9.02, -5.38) * mm});
            skPoint(sketch, "E37.6.40.0", {"position": v(11.7, -6.75) * mm});
            skLineSegment(sketch, "E37.7.40.0", {"start": v(11.77, -6.62) * mm, "end": v(11.62, -6.88) * mm});
            skLineSegment(sketch, "E37.10.40.0", {"start": v(9.17, -5.12) * mm, "end": v(9.02, -5.38) * mm});
            skLineSegment(sketch, "E37.2.41.0", {"start": v(12.4, -5.35) * mm, "end": v(9.65, -4.13) * mm});
            skLineSegment(sketch, "E37.3.41.0", {"start": v(12.27, -5.63) * mm, "end": v(9.53, -4.4) * mm});
            skPoint(sketch, "E37.6.41.0", {"position": v(12.33, -5.5) * mm});
            skLineSegment(sketch, "E37.7.41.0", {"start": v(12.4, -5.35) * mm, "end": v(12.27, -5.63) * mm});
            skLineSegment(sketch, "E37.10.41.0", {"start": v(9.65, -4.13) * mm, "end": v(9.53, -4.4) * mm});
            skLineSegment(sketch, "E37.2.42.0", {"start": v(12.89, -4.03) * mm, "end": v(10.03, -3.1) * mm});
            skLineSegment(sketch, "E37.3.42.0", {"start": v(12.8, -4.31) * mm, "end": v(9.94, -3.39) * mm});
            skPoint(sketch, "E37.6.42.0", {"position": v(12.84, -4.17) * mm});
            skLineSegment(sketch, "E37.7.42.0", {"start": v(12.89, -4.03) * mm, "end": v(12.8, -4.31) * mm});
            skLineSegment(sketch, "E37.10.42.0", {"start": v(10.03, -3.1) * mm, "end": v(9.94, -3.39) * mm});
            skLineSegment(sketch, "E37.2.43.0", {"start": v(13.24, -2.66) * mm, "end": v(10.3, -2.04) * mm});
            skLineSegment(sketch, "E37.3.43.0", {"start": v(13.17, -2.95) * mm, "end": v(10.24, -2.33) * mm});
            skPoint(sketch, "E37.6.43.0", {"position": v(13.2, -2.8) * mm});
            skLineSegment(sketch, "E37.7.43.0", {"start": v(13.24, -2.66) * mm, "end": v(13.17, -2.95) * mm});
            skLineSegment(sketch, "E37.10.43.0", {"start": v(10.3, -2.04) * mm, "end": v(10.24, -2.33) * mm});
            skLineSegment(sketch, "E37.2.44.0", {"start": v(13.44, -1.26) * mm, "end": v(10.46, -0.95) * mm});
            skLineSegment(sketch, "E37.3.44.0", {"start": v(13.41, -1.56) * mm, "end": v(10.43, -1.25) * mm});
            skPoint(sketch, "E37.6.44.0", {"position": v(13.43, -1.41) * mm});
            skLineSegment(sketch, "E37.7.44.0", {"start": v(13.44, -1.26) * mm, "end": v(13.41, -1.56) * mm});
            skLineSegment(sketch, "E37.10.44.0", {"start": v(10.46, -0.95) * mm, "end": v(10.43, -1.25) * mm});
            skLineSegment(sketch, "E37.2.45.0", {"start": v(13.5, 0.15) * mm, "end": v(10.5, 0.15) * mm});
            skLineSegment(sketch, "E37.3.45.0", {"start": v(13.5, -0.15) * mm, "end": v(10.5, -0.15) * mm});
            skPoint(sketch, "E37.6.45.0", {"position": v(13.5, 0) * mm});
            skLineSegment(sketch, "E37.7.45.0", {"start": v(13.5, 0.15) * mm, "end": v(13.5, -0.15) * mm});
            skLineSegment(sketch, "E37.10.45.0", {"start": v(10.5, 0.15) * mm, "end": v(10.5, -0.15) * mm});
            skLineSegment(sketch, "E37.2.46.0", {"start": v(13.41, 1.56) * mm, "end": v(10.43, 1.25) * mm});
            skLineSegment(sketch, "E37.3.46.0", {"start": v(13.44, 1.26) * mm, "end": v(10.46, 0.95) * mm});
            skPoint(sketch, "E37.6.46.0", {"position": v(13.43, 1.41) * mm});
            skLineSegment(sketch, "E37.7.46.0", {"start": v(13.41, 1.56) * mm, "end": v(13.44, 1.26) * mm});
            skLineSegment(sketch, "E37.10.46.0", {"start": v(10.43, 1.25) * mm, "end": v(10.46, 0.95) * mm});
            skLineSegment(sketch, "E37.2.47.0", {"start": v(13.17, 2.95) * mm, "end": v(10.24, 2.33) * mm});
            skLineSegment(sketch, "E37.3.47.0", {"start": v(13.24, 2.66) * mm, "end": v(10.3, 2.04) * mm});
            skPoint(sketch, "E37.6.47.0", {"position": v(13.2, 2.8) * mm});
            skLineSegment(sketch, "E37.7.47.0", {"start": v(13.17, 2.95) * mm, "end": v(13.24, 2.66) * mm});
            skLineSegment(sketch, "E37.10.47.0", {"start": v(10.24, 2.33) * mm, "end": v(10.3, 2.04) * mm});
            skLineSegment(sketch, "E37.2.48.0", {"start": v(12.8, 4.31) * mm, "end": v(9.94, 3.39) * mm});
            skLineSegment(sketch, "E37.3.48.0", {"start": v(12.89, 4.03) * mm, "end": v(10.03, 3.1) * mm});
            skPoint(sketch, "E37.6.48.0", {"position": v(12.84, 4.17) * mm});
            skLineSegment(sketch, "E37.7.48.0", {"start": v(12.8, 4.31) * mm, "end": v(12.89, 4.03) * mm});
            skLineSegment(sketch, "E37.10.48.0", {"start": v(9.94, 3.39) * mm, "end": v(10.03, 3.1) * mm});
            skLineSegment(sketch, "E37.2.49.0", {"start": v(12.27, 5.63) * mm, "end": v(9.53, 4.4) * mm});
            skLineSegment(sketch, "E37.3.49.0", {"start": v(12.4, 5.35) * mm, "end": v(9.65, 4.13) * mm});
            skPoint(sketch, "E37.6.49.0", {"position": v(12.33, 5.5) * mm});
            skLineSegment(sketch, "E37.7.49.0", {"start": v(12.27, 5.63) * mm, "end": v(12.4, 5.35) * mm});
            skLineSegment(sketch, "E37.10.49.0", {"start": v(9.53, 4.4) * mm, "end": v(9.65, 4.13) * mm});
            skLineSegment(sketch, "E38.2.50.0", {"start": v(11.62, 6.88) * mm, "end": v(9.02, 5.38) * mm});
            skLineSegment(sketch, "E38.3.50.0", {"start": v(11.77, 6.62) * mm, "end": v(9.17, 5.12) * mm});
            skPoint(sketch, "E38.6.50.0", {"position": v(11.7, 6.75) * mm});
            skLineSegment(sketch, "E38.7.50.0", {"start": v(11.62, 6.88) * mm, "end": v(11.77, 6.62) * mm});
            skLineSegment(sketch, "E38.10.50.0", {"start": v(9.02, 5.38) * mm, "end": v(9.17, 5.12) * mm});
            skLineSegment(sketch, "E38.2.51.0", {"start": v(10.83, 8.06) * mm, "end": v(8.4, 6.3) * mm});
            skLineSegment(sketch, "E38.3.51.0", {"start": v(11, 7.81) * mm, "end": v(8.58, 6.05) * mm});
            skPoint(sketch, "E38.6.51.0", {"position": v(10.92, 7.94) * mm});
            skLineSegment(sketch, "E38.7.51.0", {"start": v(10.83, 8.06) * mm, "end": v(11, 7.81) * mm});
            skLineSegment(sketch, "E38.10.51.0", {"start": v(8.4, 6.3) * mm, "end": v(8.58, 6.05) * mm});
            skLineSegment(sketch, "E38.2.52.0", {"start": v(9.93, 9.14) * mm, "end": v(7.7, 7.14) * mm});
            skLineSegment(sketch, "E38.3.52.0", {"start": v(10.13, 8.92) * mm, "end": v(7.9, 6.91) * mm});
            skPoint(sketch, "E38.6.52.0", {"position": v(10.03, 9.03) * mm});
            skLineSegment(sketch, "E38.7.52.0", {"start": v(9.93, 9.14) * mm, "end": v(10.13, 8.92) * mm});
            skLineSegment(sketch, "E38.10.52.0", {"start": v(7.7, 7.14) * mm, "end": v(7.9, 6.91) * mm});
            skLineSegment(sketch, "E38.2.53.0", {"start": v(8.92, 10.13) * mm, "end": v(6.91, 7.9) * mm});
            skLineSegment(sketch, "E38.3.53.0", {"start": v(9.14, 9.93) * mm, "end": v(7.14, 7.7) * mm});
            skPoint(sketch, "E38.6.53.0", {"position": v(9.03, 10.03) * mm});
            skLineSegment(sketch, "E38.7.53.0", {"start": v(8.92, 10.13) * mm, "end": v(9.14, 9.93) * mm});
            skLineSegment(sketch, "E38.10.53.0", {"start": v(6.91, 7.9) * mm, "end": v(7.14, 7.7) * mm});
            skLineSegment(sketch, "E38.2.54.0", {"start": v(7.81, 11) * mm, "end": v(6.05, 8.58) * mm});
            skLineSegment(sketch, "E38.3.54.0", {"start": v(8.06, 10.83) * mm, "end": v(6.3, 8.4) * mm});
            skPoint(sketch, "E38.6.54.0", {"position": v(7.94, 10.92) * mm});
            skLineSegment(sketch, "E38.7.54.0", {"start": v(7.81, 11) * mm, "end": v(8.06, 10.83) * mm});
            skLineSegment(sketch, "E38.10.54.0", {"start": v(6.05, 8.58) * mm, "end": v(6.3, 8.4) * mm});
            skLineSegment(sketch, "E38.2.55.0", {"start": v(6.62, 11.77) * mm, "end": v(5.12, 9.17) * mm});
            skLineSegment(sketch, "E38.3.55.0", {"start": v(6.88, 11.62) * mm, "end": v(5.38, 9.02) * mm});
            skPoint(sketch, "E38.6.55.0", {"position": v(6.75, 11.7) * mm});
            skLineSegment(sketch, "E38.7.55.0", {"start": v(6.62, 11.77) * mm, "end": v(6.88, 11.62) * mm});
            skLineSegment(sketch, "E38.10.55.0", {"start": v(5.12, 9.17) * mm, "end": v(5.38, 9.02) * mm});
            skLineSegment(sketch, "E38.2.56.0", {"start": v(5.35, 12.4) * mm, "end": v(4.13, 9.65) * mm});
            skLineSegment(sketch, "E38.3.56.0", {"start": v(5.63, 12.27) * mm, "end": v(4.4, 9.53) * mm});
            skPoint(sketch, "E38.6.56.0", {"position": v(5.5, 12.33) * mm});
            skLineSegment(sketch, "E38.7.56.0", {"start": v(5.35, 12.4) * mm, "end": v(5.63, 12.27) * mm});
            skLineSegment(sketch, "E38.10.56.0", {"start": v(4.13, 9.65) * mm, "end": v(4.4, 9.53) * mm});
            skLineSegment(sketch, "E38.2.57.0", {"start": v(4.03, 12.89) * mm, "end": v(3.1, 10.03) * mm});
            skLineSegment(sketch, "E38.3.57.0", {"start": v(4.31, 12.8) * mm, "end": v(3.39, 9.94) * mm});
            skPoint(sketch, "E38.6.57.0", {"position": v(4.17, 12.84) * mm});
            skLineSegment(sketch, "E38.7.57.0", {"start": v(4.03, 12.89) * mm, "end": v(4.31, 12.8) * mm});
            skLineSegment(sketch, "E38.10.57.0", {"start": v(3.1, 10.03) * mm, "end": v(3.39, 9.94) * mm});
            skLineSegment(sketch, "E38.2.58.0", {"start": v(2.66, 13.24) * mm, "end": v(2.04, 10.3) * mm});
            skLineSegment(sketch, "E38.3.58.0", {"start": v(2.95, 13.17) * mm, "end": v(2.33, 10.24) * mm});
            skPoint(sketch, "E38.6.58.0", {"position": v(2.8, 13.2) * mm});
            skLineSegment(sketch, "E38.7.58.0", {"start": v(2.66, 13.24) * mm, "end": v(2.95, 13.17) * mm});
            skLineSegment(sketch, "E38.10.58.0", {"start": v(2.04, 10.3) * mm, "end": v(2.33, 10.24) * mm});
            skLineSegment(sketch, "E38.2.59.0", {"start": v(1.26, 13.44) * mm, "end": v(0.95, 10.46) * mm});
            skLineSegment(sketch, "E38.3.59.0", {"start": v(1.56, 13.41) * mm, "end": v(1.25, 10.43) * mm});
            skPoint(sketch, "E38.6.59.0", {"position": v(1.41, 13.43) * mm});
            skLineSegment(sketch, "E38.7.59.0", {"start": v(1.26, 13.44) * mm, "end": v(1.56, 13.41) * mm});
            skLineSegment(sketch, "E38.10.59.0", {"start": v(0.95, 10.46) * mm, "end": v(1.25, 10.43) * mm});
            skSolve(sketch);
        }
        {
            var Q0;
            Q0 = qSketchRegion(id + "F8", true);
            extrude(context, id + "F9", {"entities" : qUnion([Q0]), "operationType" : NewBodyOperationType.REMOVE, "oppositeDirection" : true, "depth" : 0.2 * mm, "offsetDistance" : 25 * mm});
        }
        {
            var Q0;
            {var subQ0=makeQuery(id+"F6.imprint","IMPRINT",EDGE,{"derivedFrom":sQuery(id+"F6.wireOp",EDGE,"E28.MirrorCS")});var subQ1=makeQuery(id+"F5.opRevolve","SWEPT_FACE",FACE,{"disambiguationData":[OSD([sQuery(id+"F2.wireOp",EDGE,"E11")])]});Q0=makeQuery(id+"F7.boolean.opBoolean","MERGE",EDGE,{"derivedFrom":[makeQuery(id+"F7.opExtrude","TWEAK_EDGE",EDGE,{"disambiguationData":[OD(0.0)],"derivedFrom":[subQ1,subQ0]}),makeQuery(id+"F7.opExtrude","TWEAK_EDGE",EDGE,{"disambiguationData":[OD(1.0)],"derivedFrom":[subQ1,subQ0]})]});}
            fillet(context, id + "F10", {"entities" : qUnion([Q0]), "radius" : 1 * mm, "tangentPropagation" : true, "allowEdgeOverflow" : false});
        }
        {
            var Q0;
            Q0=makeQuery(id+"F1.opExtrude","CAP_FACE",FACE,{"disambiguationData":[OSD([sQuery(id+"F0.wireOp",EDGE,"E0"),sQuery(id+"F0.wireOp",EDGE,"E1")])],"isStart":true});
            var sketch = newSketch(context, id + "F11", { "sketchPlane" : qUnion([Q0])});
            skCircle(sketch, "E39", {"center": v(0, 8) * mm, "radius": 1.25 * mm});
            skCircle(sketch, "E40", {"center": v(0, -8) * mm, "radius": 1.25 * mm});
            skLineSegment(sketch, "E41", {"start": v(0, 0) * mm, "end": v(0, 8) * mm, "construction": true});
            skLineSegment(sketch, "E42", {"start": v(0, 0) * mm, "end": v(0, -8) * mm, "construction": true});
            skSolve(sketch);
        }
        {
            var Q0;
            Q0=makeQuery(id+"F11.imprint","IMPRINT",FACE,{"disambiguationData":[TD([[makeQuery(id+"F11.imprint","IMPRINT",EDGE,{"derivedFrom":sQuery(id+"F11.wireOp",EDGE,"E39")}),1.0]])]});
            var Q1;
            Q1=makeQuery(id+"F11.imprint","IMPRINT",FACE,{"disambiguationData":[TD([[makeQuery(id+"F11.imprint","IMPRINT",EDGE,{"derivedFrom":sQuery(id+"F11.wireOp",EDGE,"E40")}),1.0]])]});
            extrude(context, id + "F12", {"entities" : qUnion([Q0, Q1]), "operationType" : NewBodyOperationType.ADD, "depth" : 2 * mm, "offsetDistance" : 25 * mm});
        }
    });
